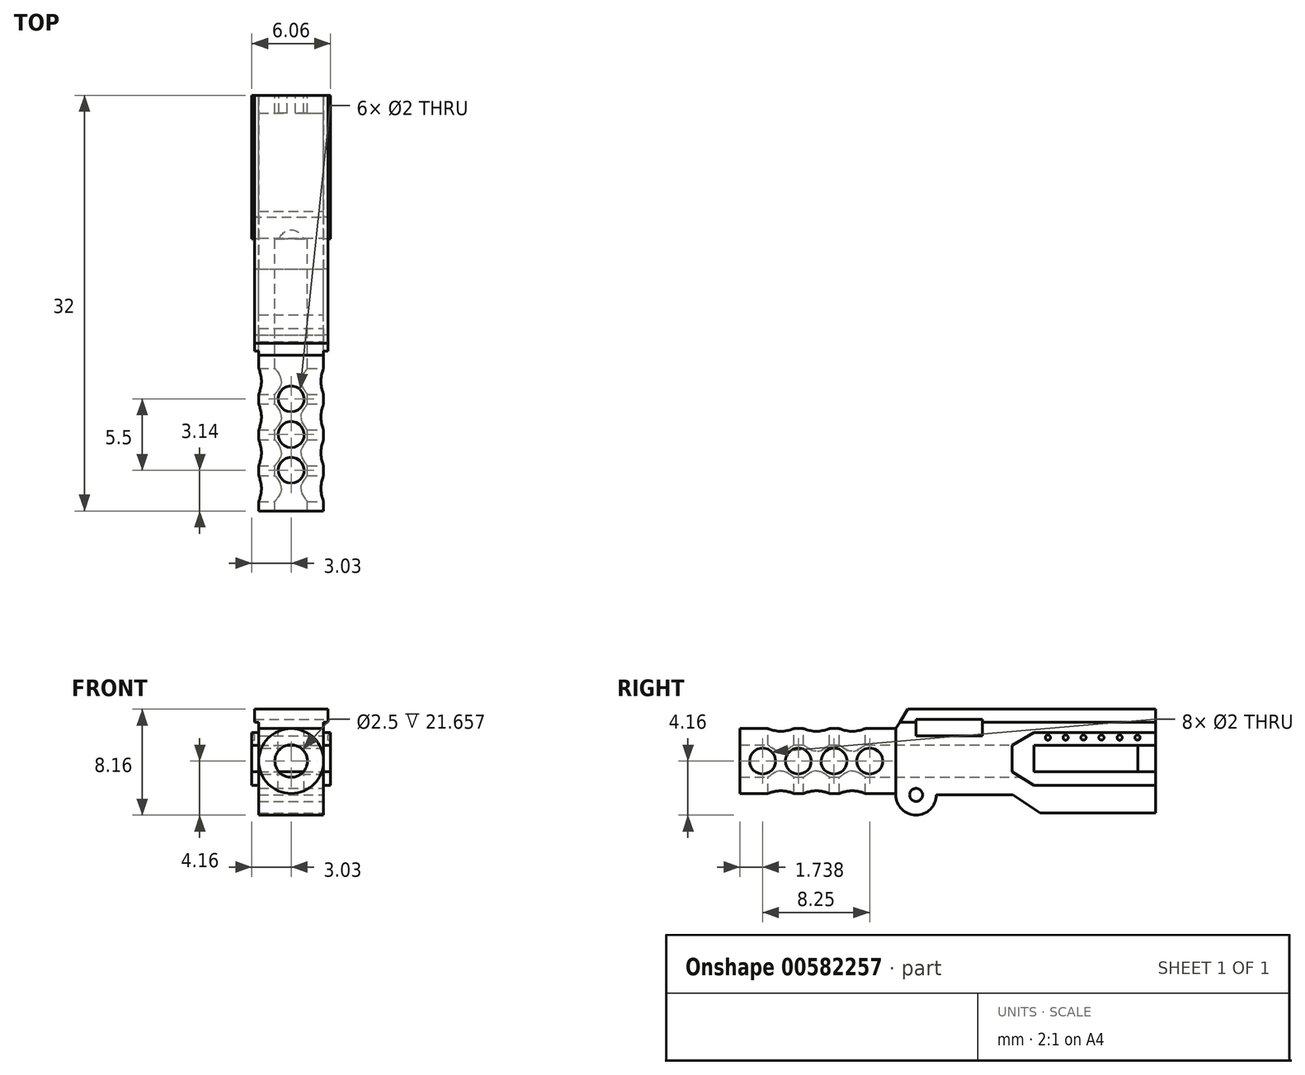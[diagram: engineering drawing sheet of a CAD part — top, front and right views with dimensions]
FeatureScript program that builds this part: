
annotation { "Feature Type Name" : "Feature", "Feature Type Description" : "" }
export const myFeature = defineFeature(function(context is Context, id is Id, definition is map)
    precondition{}
    {
        {
            var Q0;
            Q0=qCreatedBy(makeId("Front.planeOp"),FACE);
            var sketch = newSketch(context, id + "F0", { "sketchPlane" : qUnion([Q0])});
            skLineSegment(sketch, "E0.bottom", {"start": v(2.5, 4) * mm, "end": v(-2.5, 4) * mm});
            skLineSegment(sketch, "E0.top", {"start": v(2.5, -4) * mm, "end": v(-2.5, -4) * mm});
            skLineSegment(sketch, "E0.left", {"start": v(2.5, 4) * mm, "end": v(2.5, -4) * mm});
            skLineSegment(sketch, "E0.right", {"start": v(-2.5, 4) * mm, "end": v(-2.5, -4) * mm});
            skPoint(sketch, "E0.middle", {"position": v(0, 0) * mm});
            skSolve(sketch);
        }
        {
            var Q0;
            Q0=makeQuery(id+"F0.imprint","IMPRINT",FACE,{"disambiguationData":[TD([[makeQuery(id+"F0.imprint","IMPRINT",EDGE,{"derivedFrom":sQuery(id+"F0.wireOp",EDGE,"E0.bottom")}),1.0]])]});
            extrude(context, id + "F1", {"entities" : qUnion([Q0]), "depth" : 20 * mm, "offsetDistance" : 25 * mm});
        }
        {
            var Q0;
            Q0=makeQuery(id+"F1.opExtrude","CAP_FACE",FACE,{"disambiguationData":[OSD([sQuery(id+"F0.wireOp",EDGE,"E0.bottom"),sQuery(id+"F0.wireOp",EDGE,"E0.top"),sQuery(id+"F0.wireOp",EDGE,"E0.left"),sQuery(id+"F0.wireOp",EDGE,"E0.right")])],"isStart":false});
            var sketch = newSketch(context, id + "F2", { "sketchPlane" : qUnion([Q0])});
            skCircle(sketch, "E1", {"center": v(0, 0) * mm, "radius": 2.5 * mm});
            skSolve(sketch);
        }
        {
            var Q0;
            {var subQ0=sQuery(id+"F2.wireOp",EDGE,"E1");var subQ1=makeQuery(id+"F2.imprint","INTERSECT",VERTEX,{"derivedFrom":[makeQuery(id+"F1.opExtrude","CAP_EDGE",EDGE,{"disambiguationData":[OSD([sQuery(id+"F0.wireOp",EDGE,"E0.left")])],"isStart":false}),subQ0]});Q0=makeQuery(id+"F2.imprint","IMPRINT",FACE,{"disambiguationData":[TD([[makeQuery(id+"F2.imprint","IMPRINT",EDGE,{"disambiguationData":[TD([[subQ1,-1.0]])],"derivedFrom":subQ0}),1.0]])]});}
            extrude(context, id + "F3", {"entities" : qUnion([Q0]), "operationType" : NewBodyOperationType.ADD, "depth" : 12 * mm, "offsetDistance" : 25 * mm});
        }
        {
            var Q0;
            Q0=makeQuery(id+"F1.opExtrude","SWEPT_FACE",FACE,{"disambiguationData":[OSD([sQuery(id+"F0.wireOp",EDGE,"E0.left")])]});
            var sketch = newSketch(context, id + "F4", { "sketchPlane" : qUnion([Q0])});
            skLineSegment(sketch, "E2", {"start": v(-20, -4) * mm, "end": v(-20, -2.6) * mm});
            skLineSegment(sketch, "E3", {"start": v(-20, -2.6) * mm, "end": v(-10.99, -2.6) * mm});
            skLineSegment(sketch, "E4", {"start": v(-10.99, -2.6) * mm, "end": v(-8.9, -4) * mm});
            skSolve(sketch);
        }
        {
            var Q0;
            {var subQ0=sQuery(id+"F4.wireOp",EDGE,"E2");Q0=makeQuery(id+"F4.imprint","IMPRINT",FACE,{"disambiguationData":[TD([[makeQuery(id+"F4.imprint","IMPRINT",EDGE,{"derivedFrom":subQ0}),1.0]])]});}
            extrude(context, id + "F5", {"entities" : qUnion([Q0]), "operationType" : NewBodyOperationType.REMOVE, "endBound" : BoundingType.THROUGH_ALL, "oppositeDirection" : true, "depth" : 25 * mm, "offsetDistance" : 25 * mm});
        }
        {
            var Q0;
            Q0=qCreatedBy(makeId("Front.planeOp"),FACE);
            var sketch = newSketch(context, id + "F6", { "sketchPlane" : qUnion([Q0])});
            skCircle(sketch, "E5", {"center": v(0, 0) * mm, "radius": 1.25 * mm});
            skSolve(sketch);
        }
        {
            var Q0;
            Q0=makeQuery(id+"F6.imprint","IMPRINT",FACE,{"disambiguationData":[TD([[makeQuery(id+"F6.imprint","IMPRINT",EDGE,{"derivedFrom":sQuery(id+"F6.wireOp",EDGE,"E5")}),1.0]])]});
            extrude(context, id + "F7", {"entities" : qUnion([Q0]), "operationType" : NewBodyOperationType.REMOVE, "endBound" : BoundingType.THROUGH_ALL, "depth" : 25 * mm, "offsetDistance" : 25 * mm});
        }
        {
            var Q0;
            Q0=makeQuery(id+"F18.boolean.opBoolean","MERGE",FACE,{"derivedFrom":[makeQuery(id+"F1.opExtrude","SWEPT_FACE",FACE,{"disambiguationData":[OSD([sQuery(id+"F0.wireOp",EDGE,"E0.left")])]}),makeQuery(id+"F18.opExtrude","CAP_FACE",FACE,{"disambiguationData":[OSD([sQuery(id+"F4.wireOp",EDGE,"E3"),sQuery(id+"F17.wireOp",EDGE,"E26"),sQuery(id+"F17.wireOp",EDGE,"E27")])],"isStart":true})]});
            var sketch = newSketch(context, id + "F8", { "sketchPlane" : qUnion([Q0])});
            skLineSegment(sketch, "E6", {"start": v(-20, 4) * mm, "end": v(-20, 2.52) * mm});
            skLineSegment(sketch, "E7", {"start": v(-20, 2.52) * mm, "end": v(-19.07, 4) * mm});
            skLineSegment(sketch, "E8", {"start": v(-19.07, 4) * mm, "end": v(-20, 4) * mm});
            skSolve(sketch);
        }
        {
            var Q0;
            Q0=qCreatedBy(makeId("Right.planeOp"),FACE);
            var sketch = newSketch(context, id + "F9", { "sketchPlane" : qUnion([Q0])});
            skLineSegment(sketch, "E9", {"start": v(-32.01, 0) * mm, "end": v(-30.26, 0) * mm});
            skLineSegment(sketch, "E10", {"start": v(-30.26, 0) * mm, "end": v(-27.51, 0) * mm});
            skLineSegment(sketch, "E11", {"start": v(-27.51, 0) * mm, "end": v(-24.76, 0) * mm});
            skLineSegment(sketch, "E12", {"start": v(-24.76, 0) * mm, "end": v(-22.01, 0) * mm});
            skCircle(sketch, "E13", {"center": v(-30.26, 0) * mm, "radius": 1 * mm});
            skCircle(sketch, "E14", {"center": v(-27.51, 0) * mm, "radius": 1 * mm});
            skCircle(sketch, "E15", {"center": v(-24.76, 0) * mm, "radius": 1 * mm});
            skCircle(sketch, "E16", {"center": v(-22.01, 0) * mm, "radius": 1 * mm});
            skSolve(sketch);
        }
        {
            var Q0;
            Q0 = qSketchRegion(id + "F9", true);
            extrude(context, id + "F10", {"entities" : qUnion([Q0]), "operationType" : NewBodyOperationType.REMOVE, "endBound" : BoundingType.THROUGH_ALL, "oppositeDirection" : true, "depth" : 25 * mm, "offsetDistance" : 25 * mm, "hasSecondDirection" : true, "secondDirectionBound" : SecondDirectionBoundingType.THROUGH_ALL, "secondDirectionOppositeDirection" : false, "secondDirectionDepth" : 25 * mm});
        }
        {
            var Q0;
            Q0=qCreatedBy(makeId("Top.planeOp"),FACE);
            var sketch = newSketch(context, id + "F11", { "sketchPlane" : qUnion([Q0])});
            skLineSegment(sketch, "E17", {"start": v(0, -31.99) * mm, "end": v(0, -28.86) * mm});
            skLineSegment(sketch, "E18", {"start": v(0, -28.86) * mm, "end": v(0, -26.11) * mm});
            skLineSegment(sketch, "E19", {"start": v(0, -26.11) * mm, "end": v(0, -23.36) * mm});
            skCircle(sketch, "E20", {"center": v(0, -28.86) * mm, "radius": 1 * mm});
            skCircle(sketch, "E21", {"center": v(0, -26.11) * mm, "radius": 1 * mm});
            skCircle(sketch, "E22", {"center": v(0, -23.36) * mm, "radius": 1 * mm});
            skSolve(sketch);
        }
        {
            var Q0;
            Q0 = qSketchRegion(id + "F11", true);
            extrude(context, id + "F12", {"entities" : qUnion([Q0]), "operationType" : NewBodyOperationType.REMOVE, "endBound" : BoundingType.THROUGH_ALL, "oppositeDirection" : true, "depth" : 25 * mm, "offsetDistance" : 25 * mm, "hasSecondDirection" : true, "secondDirectionBound" : SecondDirectionBoundingType.THROUGH_ALL, "secondDirectionOppositeDirection" : false, "secondDirectionDepth" : 25 * mm});
        }
        {
            var Q0;
            Q0=makeQuery(id+"F1.opExtrude","SWEPT_FACE",FACE,{"disambiguationData":[OSD([sQuery(id+"F0.wireOp",EDGE,"E0.left")])]});
            var sketch = newSketch(context, id + "F13", { "sketchPlane" : qUnion([Q0])});
            skLineSegment(sketch, "E23.bottom", {"start": v(-18.44, 3.2) * mm, "end": v(-13.35, 3.2) * mm});
            skLineSegment(sketch, "E23.top", {"start": v(-18.44, 1.95) * mm, "end": v(-13.35, 1.95) * mm});
            skLineSegment(sketch, "E23.left", {"start": v(-18.44, 3.2) * mm, "end": v(-18.44, 1.95) * mm});
            skLineSegment(sketch, "E23.right", {"start": v(-13.35, 3.2) * mm, "end": v(-13.35, 1.95) * mm});
            skLineSegment(sketch, "E24.bottom", {"start": v(-1.36, 1.2) * mm, "end": v(-9.36, 1.2) * mm});
            skLineSegment(sketch, "E24.top", {"start": v(-1.36, -0.8) * mm, "end": v(-9.36, -0.8) * mm});
            skLineSegment(sketch, "E24.left", {"start": v(-1.36, 1.2) * mm, "end": v(-1.36, -0.8) * mm});
            skLineSegment(sketch, "E24.right", {"start": v(-9.36, 1.2) * mm, "end": v(-9.36, -0.8) * mm});
            skSolve(sketch);
        }
        {
            var Q0;
            Q0=makeQuery(id+"F13.imprint","IMPRINT",FACE,{"disambiguationData":[TD([[makeQuery(id+"F13.imprint","IMPRINT",EDGE,{"derivedFrom":sQuery(id+"F13.wireOp",EDGE,"E23.bottom")}),-1.0]])]});
            var Q1;
            Q1=makeQuery(id+"F13.imprint","IMPRINT",FACE,{"disambiguationData":[TD([[makeQuery(id+"F13.imprint","IMPRINT",EDGE,{"derivedFrom":sQuery(id+"F13.wireOp",EDGE,"E24.bottom")}),1.0]])]});
            extrude(context, id + "F14", {"entities" : qUnion([Q0, Q1]), "operationType" : NewBodyOperationType.REMOVE, "endBound" : BoundingType.THROUGH_ALL, "oppositeDirection" : true, "depth" : 25 * mm, "offsetDistance" : 25 * mm});
        }
        {
            var Q0;
            Q0=makeQuery(id+"F1.opExtrude","SWEPT_FACE",FACE,{"disambiguationData":[OSD([sQuery(id+"F0.wireOp",EDGE,"E0.left")])]});
            var sketch = newSketch(context, id + "F15", { "sketchPlane" : qUnion([Q0])});
            skLineSegment(sketch, "E25.bottom", {"start": v(-20, 4) * mm, "end": v(0, 4) * mm});
            skLineSegment(sketch, "E25.top", {"start": v(-20, 3) * mm, "end": v(0, 3) * mm});
            skLineSegment(sketch, "E25.left", {"start": v(-20, 4) * mm, "end": v(-20, 3) * mm});
            skLineSegment(sketch, "E25.right", {"start": v(0, 4) * mm, "end": v(0, 3) * mm});
            skSolve(sketch);
        }
        {
            var Q0;
            Q0=makeQuery(id+"F15.imprint","IMPRINT",FACE,{"disambiguationData":[TD([[makeQuery(id+"F15.imprint","IMPRINT",EDGE,{"derivedFrom":sQuery(id+"F15.wireOp",EDGE,"E25.bottom")}),-1.0]])]});
            extrude(context, id + "F16", {"entities" : qUnion([Q0]), "operationType" : NewBodyOperationType.ADD, "depth" : .33 * mm, "offsetDistance" : 25 * mm, "hasSecondDirection" : true, "secondDirectionOppositeDirection" : true, "secondDirectionDepth" : 5.33 * mm});
        }
        {
            var Q0;
            Q0=makeQuery(id+"F1.opExtrude","SWEPT_FACE",FACE,{"disambiguationData":[OSD([sQuery(id+"F0.wireOp",EDGE,"E0.left")])]});
            var sketch = newSketch(context, id + "F17", { "sketchPlane" : qUnion([Q0])});
            skCircle(sketch, "E26", {"center": v(-18.44, -2.6) * mm, "radius": 1.56 * mm});
            skCircle(sketch, "E27", {"center": v(-18.44, -2.6) * mm, "radius": 0.5 * mm});
            skSolve(sketch);
        }
        {
            var Q0;
            {var subQ3=makeQuery(id+"F5.boolean.opBoolean","COPY",EDGE,{"derivedFrom":makeQuery(id+"F5.opExtrude","CAP_EDGE",EDGE,{"disambiguationData":[OSD([sQuery(id+"F4.wireOp",EDGE,"E3")])],"isStart":true})});var subQ6=sQuery(id+"F17.wireOp",EDGE,"E27");var subQ7=makeQuery(id+"F17.imprint","INTERSECT",VERTEX,{"disambiguationData":[OD(0.0)],"derivedFrom":[subQ3,subQ6]});Q0=makeQuery(id+"F17.imprint","IMPRINT",FACE,{"disambiguationData":[TD([[makeQuery(id+"F17.imprint","IMPRINT",EDGE,{"disambiguationData":[TD([[subQ7,-1.0]])],"derivedFrom":subQ6}),-1.0]])]});}
            extrude(context, id + "F18", {"entities" : qUnion([Q0]), "operationType" : NewBodyOperationType.ADD, "oppositeDirection" : true, "depth" : 5 * mm, "offsetDistance" : 25 * mm});
        }
        {
            var Q0;
            {var subQ0=sQuery(id+"F17.wireOp",EDGE,"E27");var subQ1=makeQuery(id+"F5.boolean.opBoolean","COPY",EDGE,{"derivedFrom":makeQuery(id+"F5.opExtrude","CAP_EDGE",EDGE,{"disambiguationData":[OSD([sQuery(id+"F4.wireOp",EDGE,"E3")])],"isStart":true})});var subQ2=makeQuery(id+"F17.imprint","INTERSECT",VERTEX,{"disambiguationData":[OD(0.0)],"derivedFrom":[subQ1,subQ0]});Q0=makeQuery(id+"F17.imprint","IMPRINT",FACE,{"disambiguationData":[TD([[makeQuery(id+"F17.imprint","IMPRINT",EDGE,{"disambiguationData":[TD([[subQ2,1.0]])],"derivedFrom":subQ0}),1.0]])]});}
            extrude(context, id + "F19", {"entities" : qUnion([Q0]), "operationType" : NewBodyOperationType.REMOVE, "endBound" : BoundingType.THROUGH_ALL, "oppositeDirection" : true, "depth" : 25 * mm, "offsetDistance" : 25 * mm});
        }
        {
            var Q0;
            Q0 = qSketchRegion(id + "F8", true);
            extrude(context, id + "F20", {"entities" : qUnion([Q0]), "operationType" : NewBodyOperationType.REMOVE, "endBound" : BoundingType.THROUGH_ALL, "oppositeDirection" : true, "depth" : 25 * mm, "offsetDistance" : 25 * mm, "hasSecondDirection" : true, "secondDirectionBound" : SecondDirectionBoundingType.THROUGH_ALL, "secondDirectionOppositeDirection" : false, "secondDirectionDepth" : 25 * mm});
        }
        {
            var Q0;
            Q0=makeQuery(id+"F18.boolean.opBoolean","MERGE",FACE,{"derivedFrom":[makeQuery(id+"F1.opExtrude","SWEPT_FACE",FACE,{"disambiguationData":[OSD([sQuery(id+"F0.wireOp",EDGE,"E0.left")])]}),makeQuery(id+"F18.opExtrude","CAP_FACE",FACE,{"disambiguationData":[OSD([sQuery(id+"F4.wireOp",EDGE,"E3"),sQuery(id+"F17.wireOp",EDGE,"E26"),sQuery(id+"F17.wireOp",EDGE,"E27")])],"isStart":true})]});
            var sketch = newSketch(context, id + "F21", { "sketchPlane" : qUnion([Q0])});
            skLineSegment(sketch, "E28", {"start": v(0, -0.8) * mm, "end": v(-9.36, -0.8) * mm});
            skLineSegment(sketch, "E29", {"start": v(-9.36, -0.8) * mm, "end": v(-9.36, 1.2) * mm});
            skLineSegment(sketch, "E30", {"start": v(-9.36, 1.2) * mm, "end": v(0, 1.2) * mm});
            skLineSegment(sketch, "E31", {"start": v(0, 1.2) * mm, "end": v(0, 2.2) * mm});
            skLineSegment(sketch, "E32", {"start": v(0, 2.2) * mm, "end": v(-9.36, 2.2) * mm});
            skLineSegment(sketch, "E33", {"start": v(-9.36, 2.2) * mm, "end": v(-11.05, 1.2) * mm});
            skLineSegment(sketch, "E34", {"start": v(-11.05, 1.2) * mm, "end": v(-11.05, -0.8) * mm});
            skLineSegment(sketch, "E35", {"start": v(0, -0.8) * mm, "end": v(0, -1.86) * mm});
            skLineSegment(sketch, "E36", {"start": v(0, -1.86) * mm, "end": v(-9.36, -1.86) * mm});
            skLineSegment(sketch, "E37", {"start": v(-9.36, -1.86) * mm, "end": v(-11.05, -0.8) * mm});
            skSolve(sketch);
        }
        {
            var Q0;
            {var subQ8=sQuery(id+"F21.wireOp",EDGE,"E29");Q0=makeQuery(id+"F21.imprint","IMPRINT",FACE,{"disambiguationData":[TD([[makeQuery(id+"F21.imprint","IMPRINT",EDGE,{"derivedFrom":subQ8}),-1.0]])]});}
            extrude(context, id + "F22", {"entities" : qUnion([Q0]), "operationType" : NewBodyOperationType.ADD, "depth" : .33 * mm, "offsetDistance" : 25 * mm, "hasSecondDirection" : true, "secondDirectionOppositeDirection" : true, "secondDirectionDepth" : 5.33 * mm});
        }
        {
            var Q0;
            Q0=makeQuery(id+"F22.opExtrude","CAP_FACE",FACE,{"disambiguationData":[OSD([sQuery(id+"F21.wireOp",EDGE,"E28"),sQuery(id+"F21.wireOp",EDGE,"E29"),sQuery(id+"F21.wireOp",EDGE,"E30"),sQuery(id+"F21.wireOp",EDGE,"E31"),sQuery(id+"F21.wireOp",EDGE,"E32"),sQuery(id+"F21.wireOp",EDGE,"E33"),sQuery(id+"F21.wireOp",EDGE,"E34"),sQuery(id+"F21.wireOp",EDGE,"E35"),sQuery(id+"F21.wireOp",EDGE,"E36"),sQuery(id+"F21.wireOp",EDGE,"E37")])],"isStart":false});
            var sketch = newSketch(context, id + "F23", { "sketchPlane" : qUnion([Q0])});
            skLineSegment(sketch, "E38", {"start": v(0, 1.2) * mm, "end": v(0, 1.7) * mm});
            skLineSegment(sketch, "E39", {"start": v(0, -0.8) * mm, "end": v(0, -1.34) * mm});
            skCircle(sketch, "E40", {"center": v(-1.4, -1.34) * mm, "radius": 0.2 * mm});
            skCircle(sketch, "E41", {"center": v(-2.77, -1.33) * mm, "radius": 0.2 * mm});
            skCircle(sketch, "E42", {"center": v(-4.18, -1.34) * mm, "radius": 0.2 * mm});
            skCircle(sketch, "E43", {"center": v(-5.55, -1.34) * mm, "radius": 0.2 * mm});
            skCircle(sketch, "E44", {"center": v(-6.93, -1.33) * mm, "radius": 0.2 * mm});
            skCircle(sketch, "E45", {"center": v(-8.3, -1.33) * mm, "radius": 0.2 * mm});
            skCircle(sketch, "E46.MirrorC", {"center": v(-8.3, 1.8) * mm, "radius": 0.2 * mm});
            skCircle(sketch, "E47.MirrorC", {"center": v(-6.93, 1.8) * mm, "radius": 0.2 * mm});
            skCircle(sketch, "E48.MirrorC", {"center": v(-5.55, 1.8) * mm, "radius": 0.2 * mm});
            skCircle(sketch, "E49.MirrorC", {"center": v(-4.18, 1.8) * mm, "radius": 0.2 * mm});
            skCircle(sketch, "E50.MirrorC", {"center": v(-2.77, 1.8) * mm, "radius": 0.2 * mm});
            skCircle(sketch, "E51.MirrorC", {"center": v(-1.4, 1.8) * mm, "radius": 0.2 * mm});
            skSolve(sketch);
        }
        {
            var Q0;
            Q0=makeQuery(id+"F23.imprint","IMPRINT",FACE,{"disambiguationData":[TD([[makeQuery(id+"F23.imprint","IMPRINT",EDGE,{"derivedFrom":sQuery(id+"F23.wireOp",EDGE,"E46.MirrorC")}),-1.0]])]});
            var Q1;
            Q1=makeQuery(id+"F23.imprint","IMPRINT",FACE,{"disambiguationData":[TD([[makeQuery(id+"F23.imprint","IMPRINT",EDGE,{"derivedFrom":sQuery(id+"F23.wireOp",EDGE,"E47.MirrorC")}),-1.0]])]});
            var Q2;
            Q2=makeQuery(id+"F23.imprint","IMPRINT",FACE,{"disambiguationData":[TD([[makeQuery(id+"F23.imprint","IMPRINT",EDGE,{"derivedFrom":sQuery(id+"F23.wireOp",EDGE,"E48.MirrorC")}),-1.0]])]});
            var Q3;
            Q3=makeQuery(id+"F23.imprint","IMPRINT",FACE,{"disambiguationData":[TD([[makeQuery(id+"F23.imprint","IMPRINT",EDGE,{"derivedFrom":sQuery(id+"F23.wireOp",EDGE,"E49.MirrorC")}),-1.0]])]});
            var Q4;
            Q4=makeQuery(id+"F23.imprint","IMPRINT",FACE,{"disambiguationData":[TD([[makeQuery(id+"F23.imprint","IMPRINT",EDGE,{"derivedFrom":sQuery(id+"F23.wireOp",EDGE,"E51.MirrorC")}),-1.0]])]});
            var Q5;
            Q5=makeQuery(id+"F23.imprint","IMPRINT",FACE,{"disambiguationData":[TD([[makeQuery(id+"F23.imprint","IMPRINT",EDGE,{"derivedFrom":sQuery(id+"F23.wireOp",EDGE,"E50.MirrorC")}),-1.0]])]});
            var Q6;
            Q6=makeQuery(id+"F23.imprint","IMPRINT",FACE,{"disambiguationData":[TD([[makeQuery(id+"F23.imprint","IMPRINT",EDGE,{"derivedFrom":sQuery(id+"F23.wireOp",EDGE,"E43")}),1.0]])]});
            var Q7;
            Q7=makeQuery(id+"F23.imprint","IMPRINT",FACE,{"disambiguationData":[TD([[makeQuery(id+"F23.imprint","IMPRINT",EDGE,{"derivedFrom":sQuery(id+"F23.wireOp",EDGE,"E44")}),1.0]])]});
            var Q8;
            Q8=makeQuery(id+"F23.imprint","IMPRINT",FACE,{"disambiguationData":[TD([[makeQuery(id+"F23.imprint","IMPRINT",EDGE,{"derivedFrom":sQuery(id+"F23.wireOp",EDGE,"E45")}),1.0]])]});
            var Q9;
            Q9=makeQuery(id+"F23.imprint","IMPRINT",FACE,{"disambiguationData":[TD([[makeQuery(id+"F23.imprint","IMPRINT",EDGE,{"derivedFrom":sQuery(id+"F23.wireOp",EDGE,"E40")}),1.0]])]});
            var Q10;
            Q10=makeQuery(id+"F23.imprint","IMPRINT",FACE,{"disambiguationData":[TD([[makeQuery(id+"F23.imprint","IMPRINT",EDGE,{"derivedFrom":sQuery(id+"F23.wireOp",EDGE,"E41")}),1.0]])]});
            var Q11;
            Q11=makeQuery(id+"F23.imprint","IMPRINT",FACE,{"disambiguationData":[TD([[makeQuery(id+"F23.imprint","IMPRINT",EDGE,{"derivedFrom":sQuery(id+"F23.wireOp",EDGE,"E42")}),1.0]])]});
            extrude(context, id + "F24", {"entities" : qUnion([Q0, Q1, Q2, Q3, Q4, Q5, Q6, Q7, Q8, Q9, Q10, Q11]), "operationType" : NewBodyOperationType.ADD, "depth" : .2 * mm, "offsetDistance" : 25 * mm, "hasSecondDirection" : true, "secondDirectionOppositeDirection" : true, "secondDirectionDepth" : 5.86 * mm});
        }
    });
